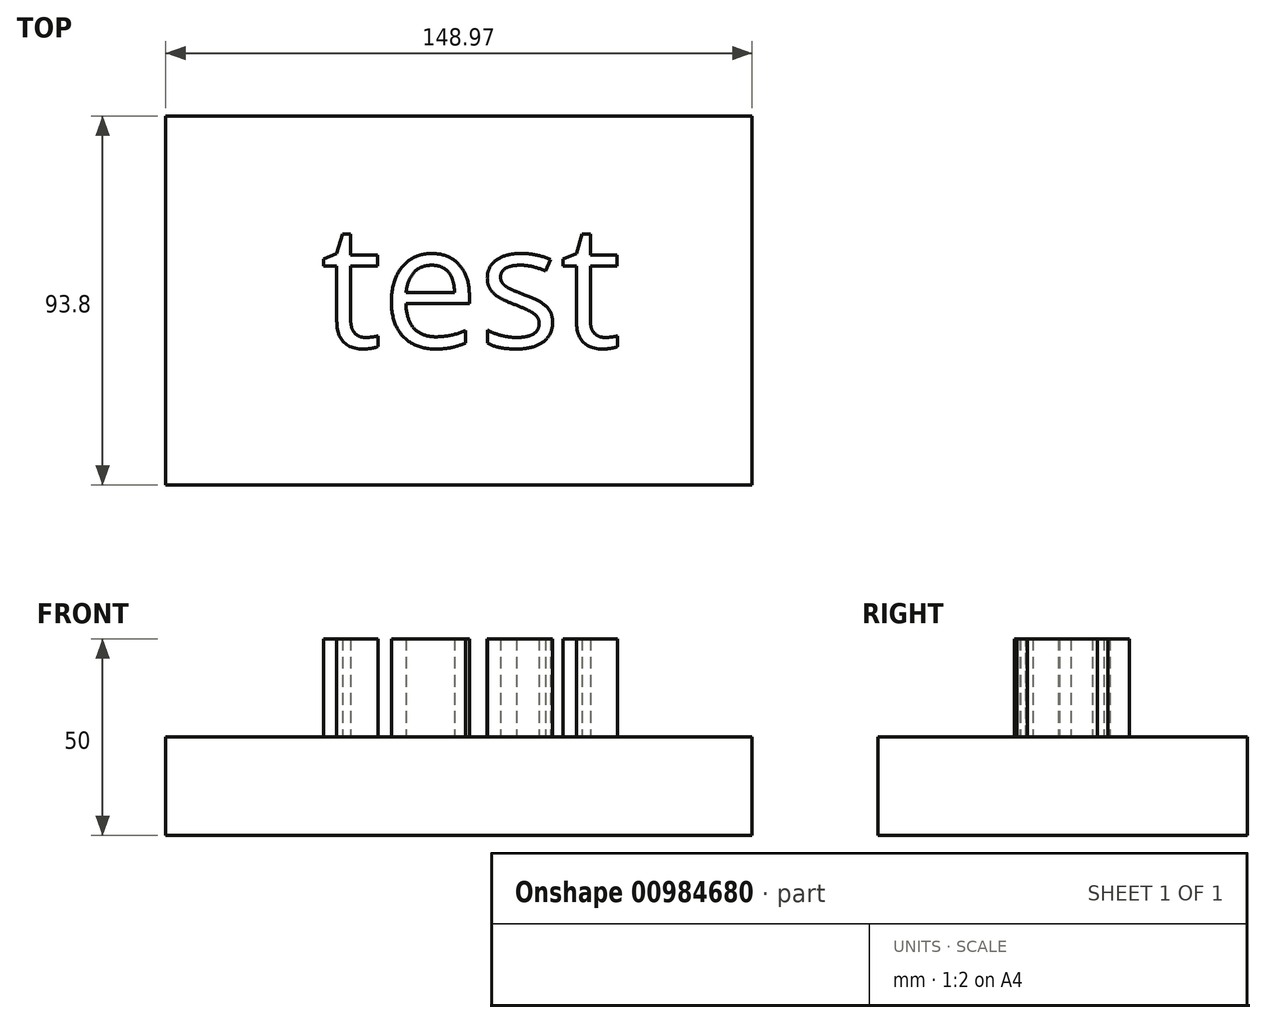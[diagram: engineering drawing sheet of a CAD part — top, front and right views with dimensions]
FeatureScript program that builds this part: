
annotation { "Feature Type Name" : "Feature", "Feature Type Description" : "" }
export const myFeature = defineFeature(function(context is Context, id is Id, definition is map)
    precondition{}
    {
        {
            var Q0;
            Q0=qCreatedBy(makeId("Top.planeOp"),FACE);
            var sketch = newSketch(context, id + "F0", { "sketchPlane" : qUnion([Q0])});
            skLineSegment(sketch, "E0.bottom", {"start": v(-61.85, 37.1) * mm, "end": v(87.12, 37.1) * mm});
            skLineSegment(sketch, "E0.top", {"start": v(-61.85, -56.71) * mm, "end": v(87.12, -56.71) * mm});
            skLineSegment(sketch, "E0.left", {"start": v(-61.85, 37.1) * mm, "end": v(-61.85, -56.71) * mm});
            skLineSegment(sketch, "E0.right", {"start": v(87.12, 37.1) * mm, "end": v(87.12, -56.71) * mm});
            skSolve(sketch);
        }
        {
            var Q0;
            Q0=makeQuery(id+"F0.imprint","IMPRINT",FACE,{"disambiguationData":[TD([[makeQuery(id+"F0.imprint","IMPRINT",EDGE,{"derivedFrom":sQuery(id+"F0.wireOp",EDGE,"1ae575f1-e6bb-48d1-92d7-db11b3046bf6.sketch_text.stroke-33")}),1.0]])]});
            var Q1;
            Q1=makeQuery(id+"F0.imprint","IMPRINT",FACE,{"disambiguationData":[TD([[makeQuery(id+"F0.imprint","IMPRINT",EDGE,{"derivedFrom":sQuery(id+"F0.wireOp",EDGE,"E0.bottom")}),-1.0]])]});
            extrude(context, id + "F1", {"entities" : qUnion([Q0, Q1]), "depth" : 25 * mm, "offsetDistance" : 25 * mm});
        }
        {
            var Q0;
            Q0=makeQuery(id+"F1.opExtrude","CAP_FACE",FACE,{"disambiguationData":[OSD([sQuery(id+"F0.wireOp",EDGE,"E0.bottom"),sQuery(id+"F0.wireOp",EDGE,"E0.top"),sQuery(id+"F0.wireOp",EDGE,"E0.left"),sQuery(id+"F0.wireOp",EDGE,"E0.right")])],"isStart":false});
            var sketch = newSketch(context, id + "F2", { "sketchPlane" : qUnion([Q0])});
            skText(sketch, "E1", { "text": "test\n", "fontName": "OpenSans-Regular.ttf"});
            const initialGuessF2  = {"E1": [-0.02241, -0.02168, 1, 0, 0.0315]};
            skSetInitialGuess(sketch, initialGuessF2);
            skSolve(sketch);
        }
        {
            var Q0;
            Q0=makeQuery(id+"F2.imprint","IMPRINT",FACE,{"disambiguationData":[TD([[makeQuery(id+"F2.imprint","IMPRINT",EDGE,{"derivedFrom":sQuery(id+"F2.wireOp",EDGE,"E1.sketch_text.stroke-0")}),-1.0]])]});
            var Q1;
            Q1=makeQuery(id+"F2.imprint","IMPRINT",FACE,{"disambiguationData":[TD([[makeQuery(id+"F2.imprint","IMPRINT",EDGE,{"derivedFrom":sQuery(id+"F2.wireOp",EDGE,"E1.sketch_text.stroke-19")}),-1.0]])]});
            var Q2;
            Q2=makeQuery(id+"F2.imprint","IMPRINT",FACE,{"disambiguationData":[TD([[makeQuery(id+"F2.imprint","IMPRINT",EDGE,{"derivedFrom":sQuery(id+"F2.wireOp",EDGE,"E1.sketch_text.stroke-38")}),-1.0]])]});
            var Q3;
            Q3=makeQuery(id+"F2.imprint","IMPRINT",FACE,{"disambiguationData":[TD([[makeQuery(id+"F2.imprint","IMPRINT",EDGE,{"derivedFrom":sQuery(id+"F2.wireOp",EDGE,"E1.sketch_text.stroke-63")}),-1.0]])]});
            extrude(context, id + "F3", {"entities" : qUnion([Q0, Q1, Q2, Q3]), "operationType" : NewBodyOperationType.ADD, "depth" : 25 * mm, "offsetDistance" : 25 * mm});
        }
    });
